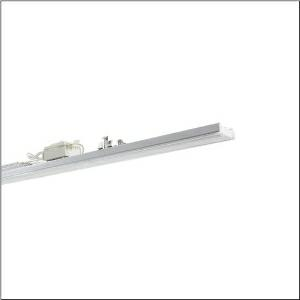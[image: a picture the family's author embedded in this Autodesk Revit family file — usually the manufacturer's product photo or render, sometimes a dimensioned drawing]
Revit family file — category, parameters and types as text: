
# Revit family: licross_r__21_recessed_ho_52te12dv4l2m3s_586b
name_source: partatom
category: Lighting Fixtures
units: mm (PartAtom-declared; Revit-internal decimal feet)

## family parameters
Cut with Voids When Loaded = No
Host = Face
Light Source = No
Part Type = Normal
Room Calculation Point = No
Round Connector Dimension = Use Diameter
Shared = No

## types (1)
- --- (1 x LED, 910 lm, 6.4 W, 4000K)
    Apparent Load = 6 VA
    CIE Flux Codes = 69 91 98 100 100
    Color Rendering = 80
    Color Temperature = 4000K
    Default Elevation = 1800 mm
    Description = Licross® 21 Recessed HO, luminaire insert, of sheet steel, galvanised, coil coated, white, length: 2.250mm, width: 66mm, height: 67mm, LED rated luminous flux: 22.710lm, light colour: 840, control gear: DALI 2 (for two DALI lines), with plug, 6-pole, with phase selection, for trunking rail, 14-core, mains connection: 220..240V, AC, 50/60Hz, rated input power: 129W, for trunking rail, 14-core, halogen-free wiring, for emergency light function, converter,control gear: single battery element, battery: LiFePO4, 9Ah, primary optical cover: cover, of PMMA, light emission: direct distribution, primary light characteristic: symmetric, protection rating (complete): IP54, insulation class (complete): insulation class I (protective earthing), certification: CE, UKCA, protection symbol: D if used in an environment with non-conductive dust loads with corresponding accessories, impact resistance: IK06, permissible ambient temperature for indoor applications: +5..+30°C, standard: EN 60598-2-22, LABS conformity tested according to VDMA 24364:2018-05, reducing of maximum allowable ambient temperature of 5°C with ceiling mounting, corresponds to IFS (International Featured Standards) requirements for safety and quality in the food industry, packaging unit: 1 piece
    Height = 58 mm
    Lamp = 1 x LED
    Lamp Light Flux = 910 lm
    Lamp Power = 6.4 W
    Lamp count = 1
    Length = 2250 mm
    Luminous efficacy = 142 lm/W
    Manufacturer = Siteco
    ModVariant = No
    Model = 52TE12DV4L2M3S
    Mounting Place = Ceiling
    Mounting Type = Pendant
    Number of Poles = 1
    OnlyDefault = Yes
    Power Factor = 1
    Product Name = Licross® 21 Recessed HO
    Product group = luminaire insert
    ProductGroupID = 902
    Protection Class = Protection class I
    Protection Degree = IP 54
    RLX_Detail_Level = 1
    RLX_Emergency_Light_Flux = 0 lm
    RLX_Emergency_Type = 0
    RLX_Emergency_Type_DB = No
    RlxData = <blob elided: 29929 chars, md5=e93e4bf1>
    Socket = socket
    Standby Power = 0 W
    System Light Flux = 910 lm
    System Power = 6 W
    Type Comments = : emergency light operation: 3 h
    Type Image = l_1296930.jpg
    URL = http://relux.com
    VarID = @adj_109334
    Voltage = 0 V
    Weight = 0.00 kg
    Width = 66 mm

## geometry (parser evidence)
native form markers: Blend x4, Sweep x10
no freeform markers — native parametric forms only
